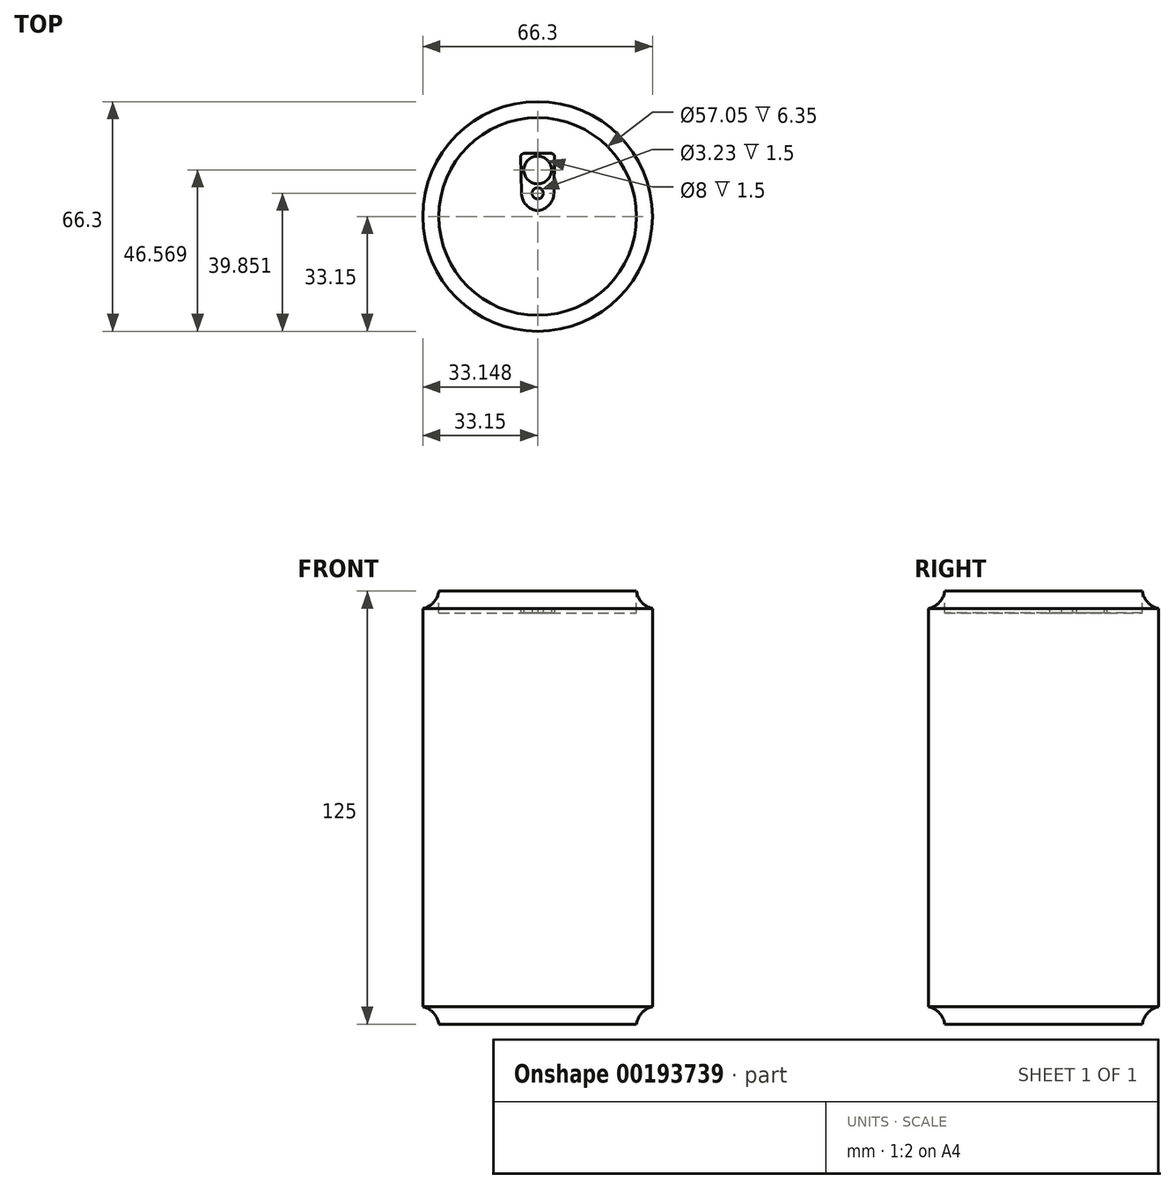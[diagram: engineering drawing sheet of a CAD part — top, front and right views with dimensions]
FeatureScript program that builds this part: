
annotation { "Feature Type Name" : "Feature", "Feature Type Description" : "" }
export const myFeature = defineFeature(function(context is Context, id is Id, definition is map)
    precondition{}
    {
        {
            var Q0;
            Q0=qCreatedBy(makeId("Top.planeOp"),FACE);
            var sketch = newSketch(context, id + "F0", { "sketchPlane" : qUnion([Q0])});
            skCircle(sketch, "E0", {"center": v(0, 0) * mm, "radius": 33.15 * mm});
            skSolve(sketch);
        }
        {
            var Q0;
            Q0=makeQuery(id+"F0.imprint","IMPRINT",FACE,{"disambiguationData":[TD([[makeQuery(id+"F0.imprint","IMPRINT",EDGE,{"derivedFrom":sQuery(id+"F0.wireOp",EDGE,"E0")}),1.0]])]});
            extrude(context, id + "F1", {"entities" : qUnion([Q0]), "endBound" : BoundingType.SYMMETRIC, "depth" : 115 * mm});
        }
        {
            var Q0;
            Q0=makeQuery(id+"F1.opExtrude","CAP_FACE",FACE,{"disambiguationData":[OSD([sQuery(id+"F0.wireOp",EDGE,"E0")])],"isStart":false});
            var sketch = newSketch(context, id + "F2", { "sketchPlane" : qUnion([Q0])});
            skCircle(sketch, "E1", {"center": v(0, 0) * mm, "radius": 28.52 * mm});
            skFitSpline(sketch, "E2", {"points": [v(27.54, 7.41) * mm, v(32.29, 7.52) * mm], "startDerivative": vector(4.71, 0.1) * mm, "endDerivative": vector(4.71, 0.1) * mm});
            skArc(sketch, "E3", {"start": v(0, 7.75) * mm, "mid": v(4, 11.75) * mm, "end": v(0, 15.75) * mm});
            skLineSegment(sketch, "E4", {"start": v(0, 16.6) * mm, "end": v(3.67, 16.6) * mm});
            skArc(sketch, "E5", {"start": v(4.9, 15.83) * mm, "mid": v(4.4, 16.4) * mm, "end": v(3.67, 16.6) * mm});
            skLineSegment(sketch, "E6", {"start": v(4.9, 15.83) * mm, "end": v(4.7, 5.1) * mm});
            skArc(sketch, "E7", {"start": v(0, 0) * mm, "mid": v(3.31, 1.67) * mm, "end": v(4.7, 5.1) * mm});
            skPoint(sketch, "E8.end.orphan", {"position": v(4.9, 4.22) * mm});
            skArc(sketch, "E9", {"start": v(0, 3.42) * mm, "mid": v(1.61, 5.03) * mm, "end": v(0, 6.64) * mm});
            skLineSegment(sketch, "E10", {"start": v(0, 18.72) * mm, "end": v(0, -1.65) * mm, "construction": true});
            skLineSegment(sketch, "E11.MirrorCS", {"start": v(0, 16.6) * mm, "end": v(-3.67, 16.6) * mm});
            skArc(sketch, "E12.MirrorCS", {"start": v(-4.9, 15.83) * mm, "mid": v(-4.4, 16.4) * mm, "end": v(-3.67, 16.6) * mm});
            skLineSegment(sketch, "E13.MirrorCS", {"start": v(-4.9, 15.83) * mm, "end": v(-4.7, 5.1) * mm});
            skArc(sketch, "E14.MirrorCS", {"start": v(0, 7.75) * mm, "mid": v(-4, 11.75) * mm, "end": v(0, 15.75) * mm});
            skArc(sketch, "E15.MirrorCS", {"start": v(0, 3.42) * mm, "mid": v(-1.61, 5.03) * mm, "end": v(0, 6.64) * mm});
            skArc(sketch, "E16.MirrorCS", {"start": v(0, 0) * mm, "mid": v(-3.31, 1.67) * mm, "end": v(-4.7, 5.1) * mm});
            skSolve(sketch);
        }
        {
            var Q0;
            Q0=makeQuery(id+"F2.imprint","IMPRINT",FACE,{"disambiguationData":[TD([[makeQuery(id+"F2.imprint","IMPRINT",EDGE,{"derivedFrom":sQuery(id+"F2.wireOp",EDGE,"E1")}),1.0]])]});
            extrude(context, id + "F3", {"entities" : qUnion([Q0]), "operationType" : NewBodyOperationType.ADD, "depth" : 5 * mm});
        }
        {
            var Q0;
            Q0=qCreatedBy(makeId("Front.planeOp"),FACE);
            var sketch = newSketch(context, id + "F4", { "sketchPlane" : qUnion([Q0])});
            skFitSpline(sketch, "E17", {"points": [v(28.52, 62.5) * mm, v(33.15, 57.5) * mm], "startDerivative": vector(1.26, -8.68) * mm, "endDerivative": vector(5.65, -0.88) * mm});
            skLineSegment(sketch, "E18", {"start": v(28.52, 62.5) * mm, "end": v(28.52, 57.5) * mm});
            skLineSegment(sketch, "E19", {"start": v(28.52, 57.5) * mm, "end": v(33.15, 57.5) * mm});
            skSolve(sketch);
        }
        {
            var Q0;
            Q0=qCreatedBy(makeId("Front.planeOp"),FACE);
            var sketch = newSketch(context, id + "F5", { "sketchPlane" : qUnion([Q0])});
            skLineSegment(sketch, "E20", {"start": v(0, 62.6) * mm, "end": v(0, 71.72) * mm});
            skSolve(sketch);
        }
        {
            var Q0;
            {var subQ0=sQuery(id+"F4.wireOp",EDGE,"E19");Q0=makeQuery(id+"F4.imprint","IMPRINT",FACE,{"disambiguationData":[TD([[makeQuery(id+"F4.imprint","IMPRINT",EDGE,{"derivedFrom":subQ0}),1.0]])]});}
            var Q1;
            Q1=sQuery(id+"F5.wireOp",EDGE,"E20");
            revolve(context, id + "F6", {"entities" : qUnion([Q0]), "axis" : qUnion([Q1]), "revolveType" : RevolveType.FULL});
        }
        {
            var Q0;
            Q0=makeQuery(id+"F6.opRevolve","SWEPT_BODY",BODY,{"disambiguationData":[OSD([sQuery(id+"F4.wireOp",EDGE,"E17"),sQuery(id+"F4.wireOp",EDGE,"E18"),sQuery(id+"F4.wireOp",EDGE,"E19")])]});
            var Q1;
            Q1=qCreatedBy(makeId("Top.planeOp"),FACE);
            mirror(context, id + "F7", {"operationType" : NewBodyOperationType.ADD, "entities" : qUnion([Q0]), "mirrorPlane" : qUnion([Q1])});
        }
        {
            var Q0;
            Q0=makeQuery(id+"F1.opExtrude","CAP_FACE",FACE,{"disambiguationData":[OSD([sQuery(id+"F0.wireOp",EDGE,"E0")])],"isStart":true});
            extrude(context, id + "F8", {"entities" : qUnion([Q0]), "operationType" : NewBodyOperationType.ADD, "depth" : 5 * mm});
        }
        {
            var Q0;
            Q0=makeQuery(id+"F3.opExtrude","CAP_FACE",FACE,{"disambiguationData":[OSD([sQuery(id+"F2.wireOp",EDGE,"E1")])],"isStart":false});
            extrude(context, id + "F9", {"entities" : qUnion([Q0]), "operationType" : NewBodyOperationType.ADD, "oppositeDirection" : true, "depth" : 3.05 * mm});
        }
        {
            var Q0;
            Q0=makeQuery(id+"F3.opExtrude","CAP_FACE",FACE,{"disambiguationData":[OSD([sQuery(id+"F2.wireOp",EDGE,"E1")])],"isStart":false});
            var sketch = newSketch(context, id + "F10", { "sketchPlane" : qUnion([Q0])});
            skCircle(sketch, "E21.0", {"center": v(0, 0) * mm, "radius": 28.52 * mm});
            skSolve(sketch);
        }
        {
            var Q0;
            Q0 = qSketchRegion(id + "F10", true);
            var Q1;
            Q1 = qSketchRegion(id + "F12", true);
            extrude(context, id + "F11", {"entities" : qUnion([Q0, Q1]), "operationType" : NewBodyOperationType.REMOVE, "oppositeDirection" : true, "depth" : 6.35 * mm});
        }
        {
            var Q0;
            Q0=qCreatedBy(makeId("Top.planeOp"),FACE);
            var sketch = newSketch(context, id + "F12", { "sketchPlane" : qUnion([Q0])});
            skSolve(sketch);
        }
        {
            var Q0;
            Q0=makeQuery(id+"F11.boolean.opBoolean","COPY",FACE,{"derivedFrom":makeQuery(id+"F11.opExtrude","CAP_FACE",FACE,{"disambiguationData":[OSD([sQuery(id+"F10.wireOp",EDGE,"E21.0")])],"isStart":false})});
            var sketch = newSketch(context, id + "F13", { "sketchPlane" : qUnion([Q0])});
            skArc(sketch, "E22", {"start": v(0, 9.42) * mm, "mid": v(4, 13.42) * mm, "end": v(0, 17.42) * mm});
            skLineSegment(sketch, "E23", {"start": v(0, 18.28) * mm, "end": v(3.67, 18.28) * mm});
            skArc(sketch, "E24", {"start": v(4.9, 17.5) * mm, "mid": v(4.4, 18.07) * mm, "end": v(3.67, 18.28) * mm});
            skLineSegment(sketch, "E25", {"start": v(4.9, 17.5) * mm, "end": v(4.7, 6.78) * mm});
            skArc(sketch, "E26", {"start": v(0, 1.67) * mm, "mid": v(3.31, 3.34) * mm, "end": v(4.7, 6.78) * mm});
            skPoint(sketch, "E27.end.orphan", {"position": v(4.9, 5.9) * mm});
            skArc(sketch, "E28", {"start": v(0, 5.09) * mm, "mid": v(1.61, 6.7) * mm, "end": v(0, 8.31) * mm});
            skLineSegment(sketch, "E29", {"start": v(0, 20.39) * mm, "end": v(0, 0.02) * mm, "construction": true});
            skLineSegment(sketch, "E30.MirrorCS", {"start": v(0, 18.28) * mm, "end": v(-3.67, 18.28) * mm});
            skArc(sketch, "E31.MirrorCS", {"start": v(-4.9, 17.5) * mm, "mid": v(-4.4, 18.07) * mm, "end": v(-3.67, 18.28) * mm});
            skLineSegment(sketch, "E32.MirrorCS", {"start": v(-4.9, 17.5) * mm, "end": v(-4.7, 6.78) * mm});
            skArc(sketch, "E33.MirrorCS", {"start": v(0, 9.42) * mm, "mid": v(-4, 13.42) * mm, "end": v(0, 17.42) * mm});
            skArc(sketch, "E34.MirrorCS", {"start": v(0, 5.09) * mm, "mid": v(-1.62, 6.7) * mm, "end": v(0, 8.31) * mm});
            skArc(sketch, "E35.MirrorCS", {"start": v(0, 1.67) * mm, "mid": v(-3.32, 3.34) * mm, "end": v(-4.7, 6.78) * mm});
            skSolve(sketch);
        }
        {
            var Q0;
            Q0=makeQuery(id+"F13.imprint","IMPRINT",FACE,{"disambiguationData":[TD([[makeQuery(id+"F13.imprint","IMPRINT",EDGE,{"derivedFrom":sQuery(id+"F13.wireOp",EDGE,"E22")}),-1.0]])]});
            extrude(context, id + "F14", {"entities" : qUnion([Q0]), "operationType" : NewBodyOperationType.ADD, "depth" : 1.5 * mm});
        }
    });
